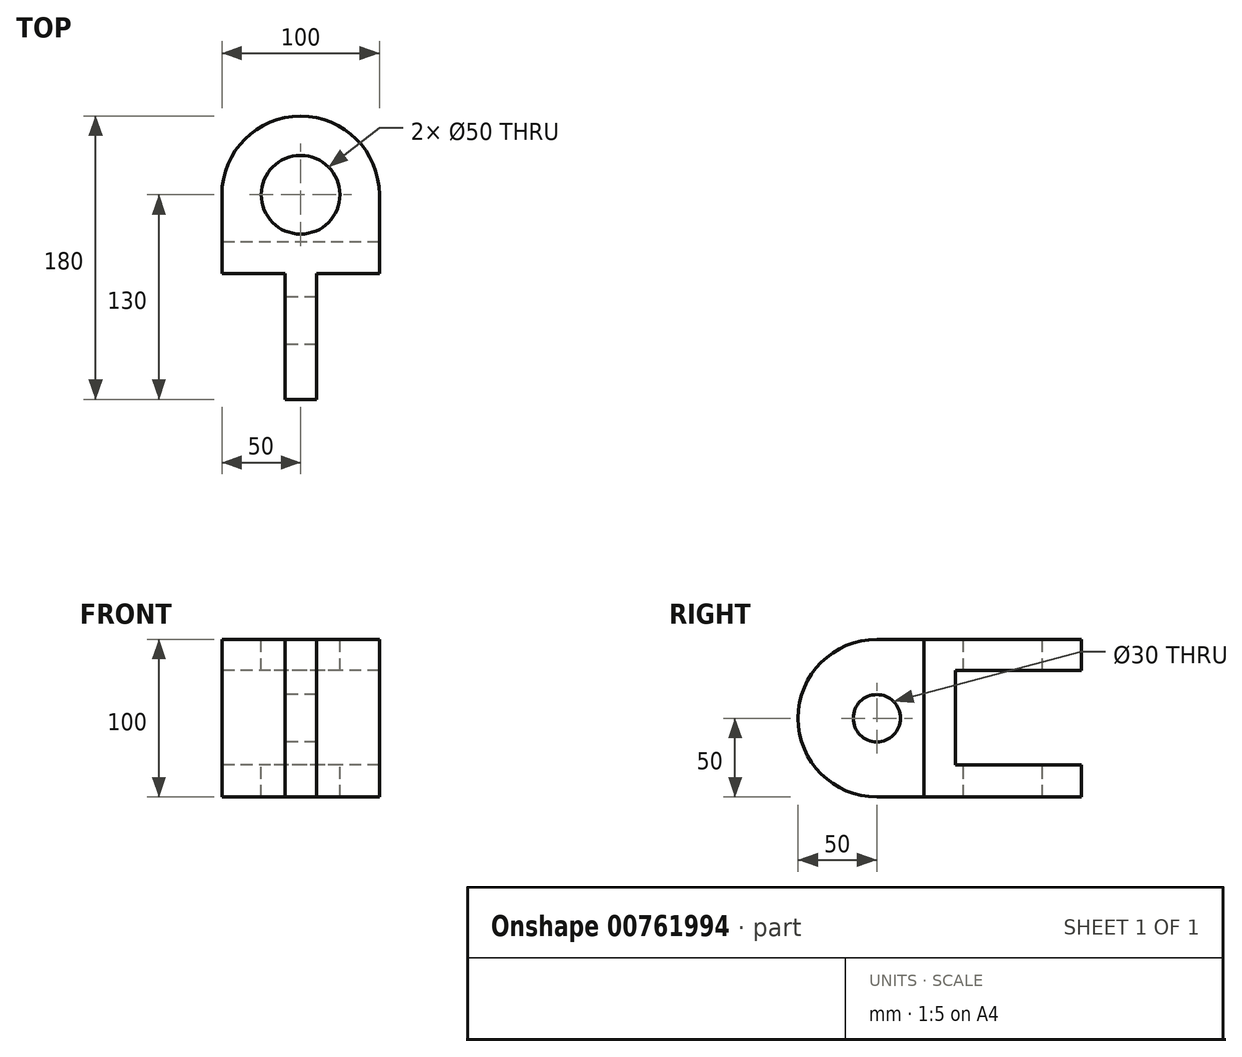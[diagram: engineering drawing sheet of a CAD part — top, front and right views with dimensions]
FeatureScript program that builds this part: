
annotation { "Feature Type Name" : "Feature", "Feature Type Description" : "" }
export const myFeature = defineFeature(function(context is Context, id is Id, definition is map)
    precondition{}
    {
        {
            var Q0;
            Q0=qCreatedBy(makeId("Top.planeOp"),FACE);
            var sketch = newSketch(context, id + "F0", { "sketchPlane" : qUnion([Q0])});
            skLineSegment(sketch, "E0.bottom", {"start": v(0, 0) * mm, "end": v(100, 0) * mm});
            skLineSegment(sketch, "E0.left", {"start": v(0, 0) * mm, "end": v(0, 50) * mm});
            skLineSegment(sketch, "E0.right", {"start": v(100, 0) * mm, "end": v(100, 50) * mm});
            skCircle(sketch, "E1", {"center": v(50, 50) * mm, "radius": 25 * mm});
            skArc(sketch, "E2", {"start": v(100, 50) * mm, "mid": v(50, 100) * mm, "end": v(0, 50) * mm});
            skLineSegment(sketch, "E3.bottom", {"start": v(40, 0) * mm, "end": v(60, 0) * mm});
            skLineSegment(sketch, "E3.top", {"start": v(40, -30) * mm, "end": v(60, -30) * mm});
            skLineSegment(sketch, "E3.left", {"start": v(40, 0) * mm, "end": v(40, -30) * mm});
            skLineSegment(sketch, "E3.right", {"start": v(60, 0) * mm, "end": v(60, -30) * mm});
            skLineSegment(sketch, "E4.top", {"start": v(40, -80) * mm, "end": v(60, -80) * mm});
            skLineSegment(sketch, "E4.left", {"start": v(40, -30) * mm, "end": v(40, -80) * mm});
            skLineSegment(sketch, "E4.right", {"start": v(60, -30) * mm, "end": v(60, -80) * mm});
            skSolve(sketch);
        }
        {
            var Q0;
            Q0=makeQuery(id+"F0.imprint","IMPRINT",FACE,{"disambiguationData":[TD([[makeQuery(id+"F0.imprint","IMPRINT",EDGE,{"derivedFrom":sQuery(id+"F0.wireOp",EDGE,"E3.top")}),-1.0]])]});
            var Q1;
            {var subQ0=sQuery(id+"F0.wireOp",EDGE,"E0.left");Q1=makeQuery(id+"F0.imprint","IMPRINT",FACE,{"disambiguationData":[TD([[makeQuery(id+"F0.imprint","IMPRINT",EDGE,{"derivedFrom":subQ0}),-1.0]])]});}
            var Q2;
            Q2=makeQuery(id+"F0.imprint","IMPRINT",FACE,{"disambiguationData":[TD([[makeQuery(id+"F0.imprint","IMPRINT",EDGE,{"derivedFrom":sQuery(id+"F0.wireOp",EDGE,"E3.top")}),1.0]])]});
            extrude(context, id + "F1", {"entities" : qUnion([Q0, Q1, Q2]), "oppositeDirection" : true, "depth" : 100 * mm, "offsetDistance" : 25 * mm});
        }
        {
            var Q0;
            Q0=makeQuery(id+"F1.opExtrude","SWEPT_FACE",FACE,{"disambiguationData":[OSD([sQuery(id+"F0.wireOp",EDGE,"E0.left")])]});
            var sketch = newSketch(context, id + "F2", { "sketchPlane" : qUnion([Q0])});
            skLineSegment(sketch, "E5.bottom", {"start": v(-20, -19.53) * mm, "end": v(-105.67, -19.53) * mm});
            skLineSegment(sketch, "E5.top", {"start": v(-20, -79.53) * mm, "end": v(-105.67, -79.53) * mm});
            skLineSegment(sketch, "E5.left", {"start": v(-20, -19.53) * mm, "end": v(-20, -79.53) * mm});
            skLineSegment(sketch, "E5.right", {"start": v(-105.67, -19.53) * mm, "end": v(-105.67, -79.53) * mm});
            skSolve(sketch);
        }
        {
            var Q0;
            {var subQ0=sQuery(id+"F2.wireOp",EDGE,"E5.left");Q0=makeQuery(id+"F2.imprint","IMPRINT",FACE,{"disambiguationData":[TD([[makeQuery(id+"F2.imprint","IMPRINT",EDGE,{"derivedFrom":subQ0}),-1.0]])]});}
            var Q1;
            {var subQ0=sQuery(id+"F2.wireOp",EDGE,"E5.right");Q1=makeQuery(id+"F2.imprint","IMPRINT",FACE,{"disambiguationData":[TD([[makeQuery(id+"F2.imprint","IMPRINT",EDGE,{"derivedFrom":subQ0}),1.0]])]});}
            extrude(context, id + "F3", {"entities" : qUnion([Q0, Q1]), "operationType" : NewBodyOperationType.REMOVE, "endBound" : BoundingType.THROUGH_ALL, "oppositeDirection" : true, "depth" : 25 * mm, "offsetDistance" : 25 * mm});
        }
        {
            var Q0;
            Q0=makeQuery(id+"F1.opExtrude","SWEPT_FACE",FACE,{"disambiguationData":[OSD([sQuery(id+"F0.wireOp",EDGE,"E3.left"),sQuery(id+"F0.wireOp",EDGE,"E4.left")])]});
            var sketch = newSketch(context, id + "F4", { "sketchPlane" : qUnion([Q0])});
            skLineSegment(sketch, "E6.bottom", {"start": v(0, 0) * mm, "end": v(30, 0) * mm});
            skLineSegment(sketch, "E6.top", {"start": v(0, -100) * mm, "end": v(30, -100) * mm});
            skLineSegment(sketch, "E6.left", {"start": v(0, 0) * mm, "end": v(0, -100) * mm});
            skCircle(sketch, "E7", {"center": v(30, -50) * mm, "radius": 15 * mm});
            skArc(sketch, "E8", {"start": v(30, -100) * mm, "mid": v(80, -50) * mm, "end": v(30, 0) * mm});
            skSolve(sketch);
        }
        {
            var Q0;
            {var subQ0=sQuery(id+"F4.wireOp",EDGE,"E8");var subQ1=sQuery(id+"F0.wireOp",EDGE,"E4.left");var subQ4=makeQuery(id+"F1.opExtrude","SWEPT_EDGE",EDGE,{"disambiguationData":[OSD([sQuery(id+"F0.wireOp",EDGE,"E4.top"),subQ1])]});var subQ5=makeQuery(id+"F4.imprint","INTERSECT",VERTEX,{"derivedFrom":[subQ4,subQ0]});Q0=makeQuery(id+"F4.imprint","IMPRINT",FACE,{"disambiguationData":[TD([[makeQuery(id+"F4.imprint","IMPRINT",EDGE,{"disambiguationData":[TD([[subQ5,-1.0]])],"derivedFrom":subQ0}),-1.0]])]});}
            var Q1;
            {var subQ0=sQuery(id+"F4.wireOp",EDGE,"E8");var subQ1=sQuery(id+"F0.wireOp",EDGE,"E4.left");var subQ4=makeQuery(id+"F1.opExtrude","SWEPT_EDGE",EDGE,{"disambiguationData":[OSD([sQuery(id+"F0.wireOp",EDGE,"E4.top"),subQ1])]});var subQ5=makeQuery(id+"F4.imprint","INTERSECT",VERTEX,{"derivedFrom":[subQ4,subQ0]});Q1=makeQuery(id+"F4.imprint","IMPRINT",FACE,{"disambiguationData":[TD([[makeQuery(id+"F4.imprint","IMPRINT",EDGE,{"disambiguationData":[TD([[subQ5,1.0]])],"derivedFrom":subQ0}),-1.0]])]});}
            extrude(context, id + "F5", {"entities" : qUnion([Q0, Q1]), "operationType" : NewBodyOperationType.REMOVE, "endBound" : BoundingType.THROUGH_ALL, "oppositeDirection" : true, "depth" : 25 * mm, "offsetDistance" : 25 * mm});
        }
        {
            var Q0;
            Q0=makeQuery(id+"F4.imprint","IMPRINT",FACE,{"disambiguationData":[TD([[makeQuery(id+"F4.imprint","IMPRINT",EDGE,{"derivedFrom":sQuery(id+"F4.wireOp",EDGE,"E7")}),1.0]])]});
            extrude(context, id + "F6", {"entities" : qUnion([Q0]), "operationType" : NewBodyOperationType.REMOVE, "endBound" : BoundingType.THROUGH_ALL, "oppositeDirection" : true, "depth" : 25 * mm, "offsetDistance" : 25 * mm});
        }
    });
